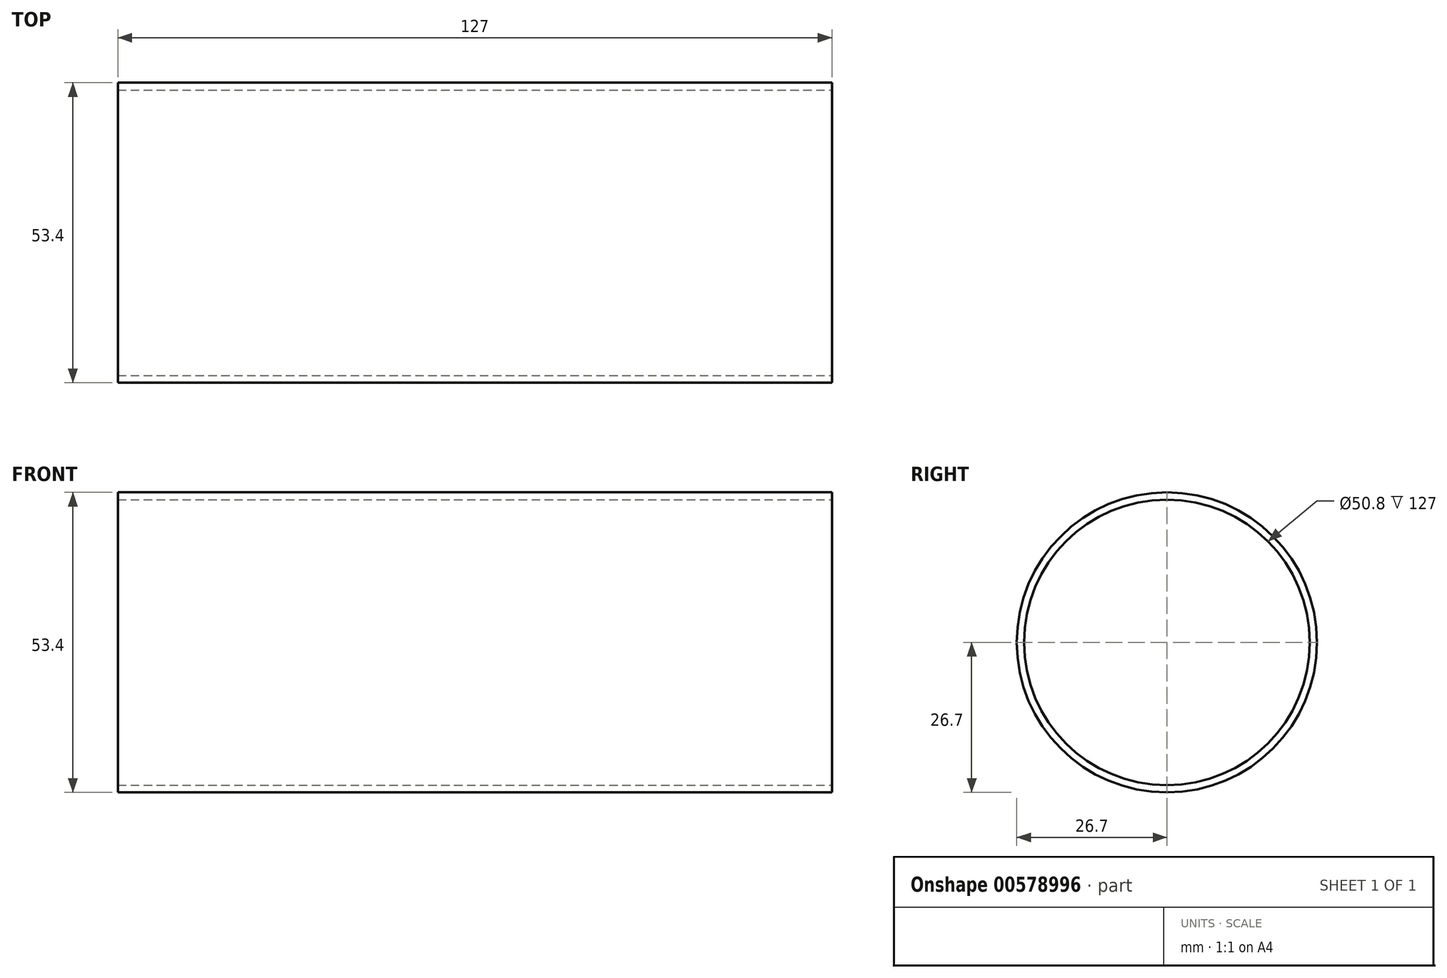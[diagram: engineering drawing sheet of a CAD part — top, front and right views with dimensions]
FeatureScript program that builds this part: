
annotation { "Feature Type Name" : "Feature", "Feature Type Description" : "" }
export const myFeature = defineFeature(function(context is Context, id is Id, definition is map)
    precondition{}
    {
        {
            var Q0;
            Q0=qCreatedBy(makeId("Right.planeOp"),FACE);
            var sketch = newSketch(context, id + "F0", { "sketchPlane" : qUnion([Q0])});
            skCircle(sketch, "E0", {"center": v(0, 0) * mm, "radius": 26.7 * mm});
            skSolve(sketch);
        }
        {
            var Q0;
            Q0 = qSketchRegion(id + "F0", true);
            extrude(context, id + "F1", {"entities" : qUnion([Q0]), "endBound" : BoundingType.SYMMETRIC, "depth" : 127 * mm, "offsetDistance" : 25.4 * mm});
        }
        {
            var Q0;
            Q0=makeQuery(id+"F1.opExtrude","CAP_FACE",FACE,{"disambiguationData":[OSD([sQuery(id+"F0.wireOp",EDGE,"E0")])],"isStart":false});
            var sketch = newSketch(context, id + "F2", { "sketchPlane" : qUnion([Q0])});
            skCircle(sketch, "E1", {"center": v(0, 0) * mm, "radius": 25.4 * mm});
            skSolve(sketch);
        }
        {
            var Q0;
            Q0 = qSketchRegion(id + "F2", true);
            extrude(context, id + "F3", {"entities" : qUnion([Q0]), "operationType" : NewBodyOperationType.REMOVE, "endBound" : BoundingType.SYMMETRIC, "oppositeDirection" : true, "depth" : 304.8 * mm, "offsetDistance" : 25.4 * mm});
        }
    });
